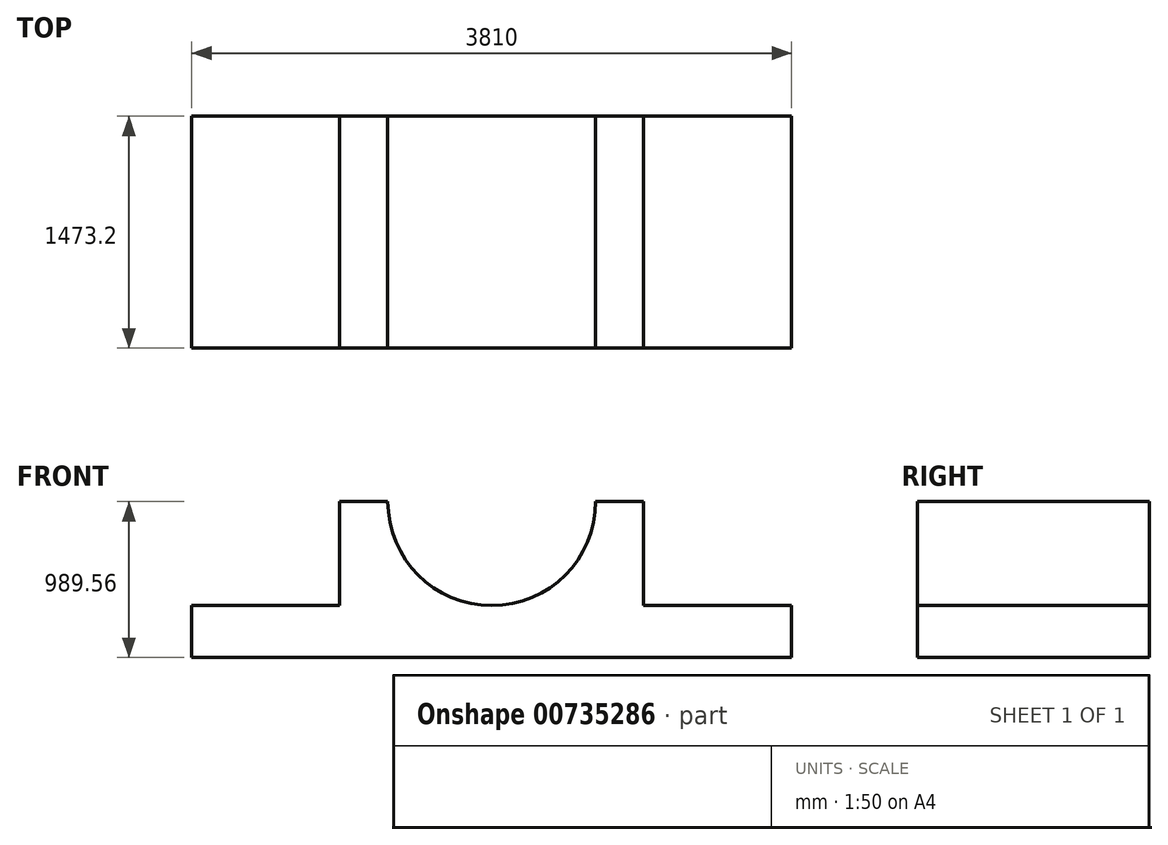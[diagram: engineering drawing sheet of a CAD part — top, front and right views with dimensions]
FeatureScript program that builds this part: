
annotation { "Feature Type Name" : "Feature", "Feature Type Description" : "" }
export const myFeature = defineFeature(function(context is Context, id is Id, definition is map)
    precondition{}
    {
        {
            var Q0;
            Q0=qCreatedBy(makeId("Front.planeOp"),FACE);
            var sketch = newSketch(context, id + "F0", { "sketchPlane" : qUnion([Q0])});
            skLineSegment(sketch, "E0.bottom", {"start": v(-530.96, 42.61) * mm, "end": v(-226.16, 42.61) * mm});
            skLineSegment(sketch, "E0.left", {"start": v(-530.96, 42.61) * mm, "end": v(-530.96, -617.79) * mm});
            skLineSegment(sketch, "E0.right", {"start": v(1399.44, 42.61) * mm, "end": v(1399.44, -617.79) * mm});
            skLineSegment(sketch, "E1", {"start": v(1399.44, -617.79) * mm, "end": v(2339.24, -617.79) * mm});
            skLineSegment(sketch, "E2", {"start": v(2339.24, -617.79) * mm, "end": v(2339.24, -946.95) * mm});
            skLineSegment(sketch, "E3", {"start": v(2339.24, -946.95) * mm, "end": v(-1470.76, -946.95) * mm});
            skLineSegment(sketch, "E4", {"start": v(-1470.76, -946.95) * mm, "end": v(-1470.76, -617.79) * mm});
            skLineSegment(sketch, "E5", {"start": v(-1470.76, -617.79) * mm, "end": v(-530.96, -617.79) * mm});
            skLineSegment(sketch, "E6", {"start": v(434.24, 42.61) * mm, "end": v(434.24, -340.59) * mm, "construction": true});
            skArc(sketch, "E7", {"start": v(-226.16, 42.61) * mm, "mid": v(434.24, -617.79) * mm, "end": v(1094.64, 42.61) * mm});
            skLineSegment(sketch, "E8.trimOffspring", {"start": v(1094.64, 42.61) * mm, "end": v(1399.44, 42.61) * mm});
            skSolve(sketch);
        }
        {
            var Q0;
            Q0=makeQuery(id+"F0.imprint","IMPRINT",FACE,{"disambiguationData":[TD([[makeQuery(id+"F0.imprint","IMPRINT",EDGE,{"derivedFrom":sQuery(id+"F0.wireOp",EDGE,"E0.bottom")}),-1.0]])]});
            extrude(context, id + "F1", {"entities" : qUnion([Q0]), "oppositeDirection" : true, "depth" : 1473.2 * mm, "offsetDistance" : 25.4 * mm});
        }
    });
